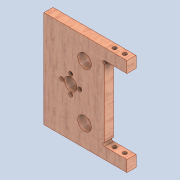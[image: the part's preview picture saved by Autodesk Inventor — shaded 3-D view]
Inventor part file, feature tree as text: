
AUTODESK INVENTOR PART (.ipt)
format: ipt  version: 2020 (Build 240168000, 168)  size: 266,240 bytes
history: native  units: mm
features: sketch x6, extrude x5, other x2, hole x1, reference x1
ambient origin geometry x8: Origin, YZ Plane, XZ Plane, XY Plane, X Axis, Y Axis, Z Axis, Center Point
bodies: Solid1 (feature_tree)
feature tree (15):
  extrude  "Extrusion1"  Depth=86.0mm
  extrude  "Extrusion4"  Depth=20.0mm
  extrude  "Extrusion5"  Depth=10.0mm TaperAngle=0.0deg
  extrude  "Extrusion6"  Depth=10.0mm TaperAngle=0.0deg
  hole  "Hole1"  [1 undecoded]
  extrude  "Extrusion7"  Depth=10.0mm TaperAngle=0.0deg
  sketch  "Sketch1"  dims[d0=73.5mm d1=86.0mm]
  sketch  "Sketch4"  dims[d2=8.0mm d3=0.0mm d19=20.0mm]
  sketch  "Sketch5"  dims[d20=66.0mm d21=10.0mm d22=0.0mm]
  reference  "Reference1"
  sketch  "Sketch6"  dims[d23=12.0mm d29=10.0mm d30=0.0mm]
  sketch  "Sketch7"  dims[d37=37.5mm d38=19.0mm]
  sketch  "Sketch8"  dims[d39=19.0mm d40=10.0mm d41=0.0mm d42=3.5mm d43=11.0mm d44=23.751158mm d46=22.0mm d47=16.0mm d48=9.0mm d49=6.0mm d50=3.5mm d51=6.0mm d52=4.0mm d53=2.0mm d54=90.0deg d55=8.0mm d56=20.594885mm d57=3.0mm d58=3.0mm d59=0.0mm d60=0.0mm]
  other  "0005-10-04 Y axis and extruder.iam"
  other  "0005-10-009.ipt:14"
note: 1 required parameter value undecoded (feature->parameter linkage not recoverable at this tier; creation-order binding heuristic only, values carry confidence <= 0.55)
